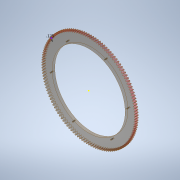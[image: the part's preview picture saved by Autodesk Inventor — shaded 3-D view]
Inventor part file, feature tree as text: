
AUTODESK INVENTOR PART (.ipt)
format: ipt  version: 2020 (Build 240168000, 168)  size: 2,173,952 bytes
history: native  units: mm (DEFAULTED — no unit token found)
features: sketch x3, hole x2, extrude x1, pattern_circular x1, projected_geometry x1, other x1
ambient origin geometry x8: Origin, YZ Plane, XZ Plane, XY Plane, X Axis, Y Axis, Z Axis, Center Point
bodies: Solid1 (feature_tree)
feature tree (9):
  extrude  "Extrusion1"  Depth=25.4mm
  hole  "Hole1"  [1 undecoded]
  hole  "Hole2"  [1 undecoded]
  pattern_circular  "Circular Pattern1"  [2 undecoded]
  sketch  "Sketch1"  dims[d0=260.35mm d1=9.652mm d2=9.525mm d3=6.35mm d4=14.3117mm d5=25.4mm d6=20.594885mm d7=273.5mm]
  sketch  "Sketch2"  dims[d8=3.9624mm d9=9.652mm d10=11.1252mm d11=6.35mm d12=14.0mm d13=13.6144mm d14=20.594885mm d15=60.0mm d16=62.831853mm]
  sketch  "Sketch3"  dims[d18=3.175mm d19=0.0mm d17=19.05mm d21=25.4mm d22=25.4mm d23=25.4mm d24=3.81mm d25=6.35mm d26=9.525mm d27=820.0mm d28=19.05mm d29=1180.0mm d30=1.5875mm d31=19.05mm d32=9.525mm]
  projected_geometry  "Projected Loop1"
  other  "Pattern10DP 130T Gear"
note: 4 required parameter values undecoded (feature->parameter linkage not recoverable at this tier; creation-order binding heuristic only, values carry confidence <= 0.55)
